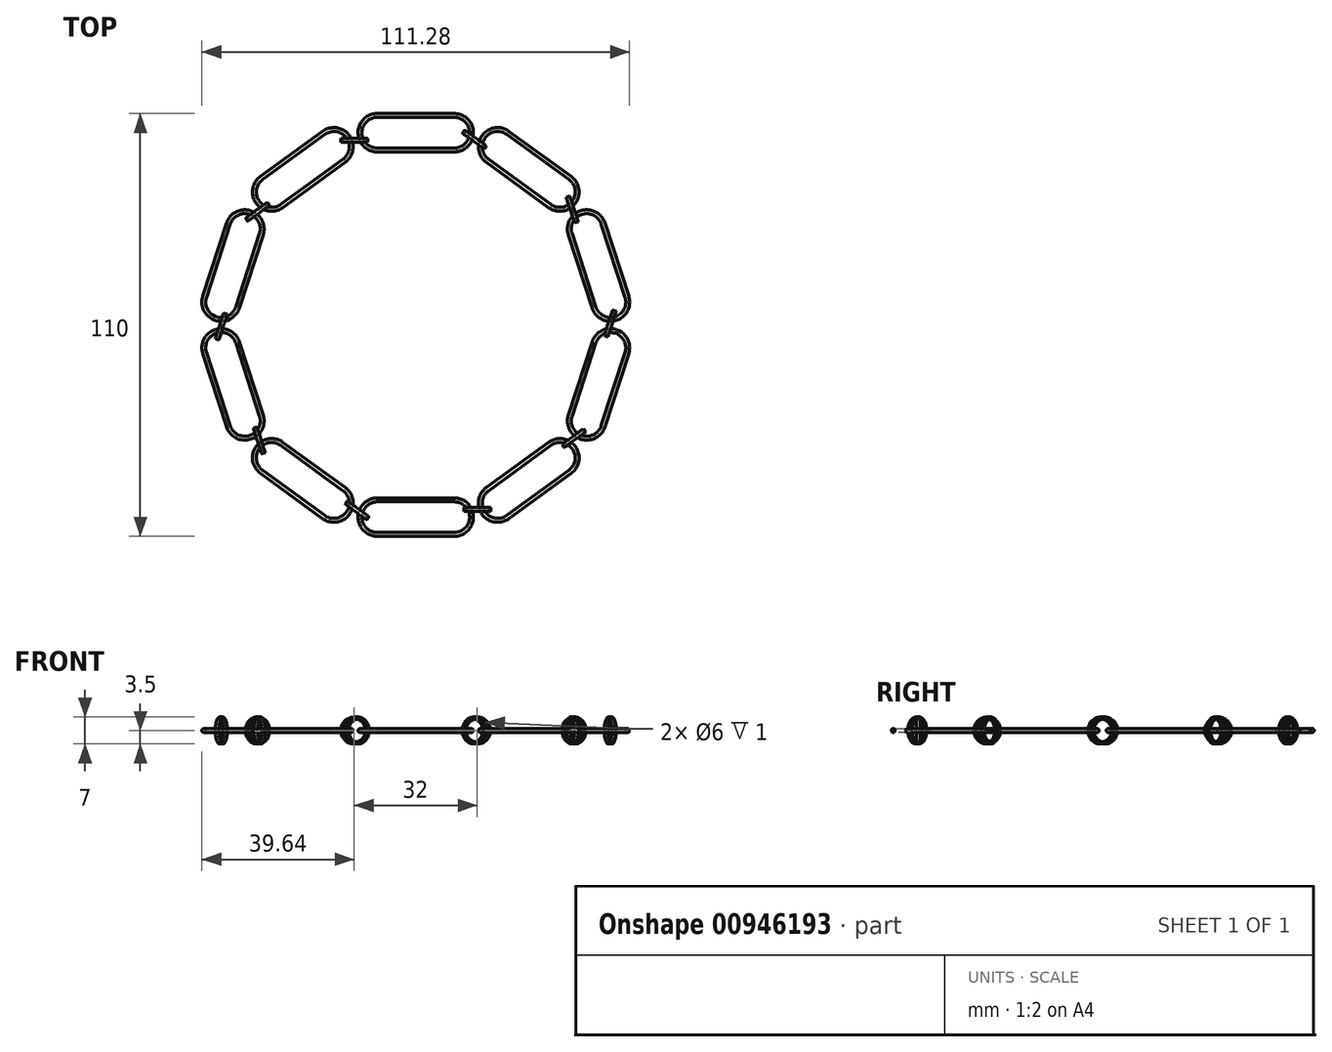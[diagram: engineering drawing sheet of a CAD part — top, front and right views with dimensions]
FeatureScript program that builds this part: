
annotation { "Feature Type Name" : "Feature", "Feature Type Description" : "" }
export const myFeature = defineFeature(function(context is Context, id is Id, definition is map)
    precondition{}
    {
        {
            var Q0;
            Q0=qCreatedBy(makeId("Top.planeOp"),FACE);
            var sketch = newSketch(context, id + "F0", { "sketchPlane" : qUnion([Q0])});
            skArc(sketch, "E0", {"start": v(-10, -45) * mm, "mid": v(-15, -50) * mm, "end": v(-10, -55) * mm});
            skArc(sketch, "E1", {"start": v(10, -55) * mm, "mid": v(15, -50) * mm, "end": v(10, -45) * mm});
            skLineSegment(sketch, "E2", {"start": v(-10, -45) * mm, "end": v(10, -45) * mm});
            skLineSegment(sketch, "E3", {"start": v(-10, -55) * mm, "end": v(10, -55) * mm});
            skLineSegment(sketch, "E4", {"start": v(-10, -50) * mm, "end": v(10, -50) * mm, "construction": true});
            skPoint(sketch, "E5", {"position": v(0, -50) * mm});
            skArc(sketch, "E6.0", {"start": v(-10, -46) * mm, "mid": v(-14, -50) * mm, "end": v(-10, -54) * mm});
            skLineSegment(sketch, "E6.1", {"start": v(-10, -46) * mm, "end": v(10, -46) * mm});
            skArc(sketch, "E6.2", {"start": v(10, -54) * mm, "mid": v(14, -50) * mm, "end": v(10, -46) * mm});
            skLineSegment(sketch, "E6.3", {"start": v(-10, -54) * mm, "end": v(10, -54) * mm});
            skSolve(sketch);
        }
        {
            var Q0;
            Q0 = qSketchRegion(id + "F0", true);
            extrude(context, id + "F1", {"entities" : qUnion([Q0]), "depth" : 1 * mm, "offsetDistance" : 25 * mm});
        }
        {
            var Q0;
            Q0=makeQuery(id+"F1.opExtrude","CAP_FACE",FACE,{"disambiguationData":[OSD([sQuery(id+"F0.wireOp",EDGE,"E0"),sQuery(id+"F0.wireOp",EDGE,"E1"),sQuery(id+"F0.wireOp",EDGE,"E2"),sQuery(id+"F0.wireOp",EDGE,"E3"),sQuery(id+"F0.wireOp",EDGE,"E6.0"),sQuery(id+"F0.wireOp",EDGE,"E6.1"),sQuery(id+"F0.wireOp",EDGE,"E6.2"),sQuery(id+"F0.wireOp",EDGE,"E6.3")])],"isStart":true});
            var Q1;
            Q1=makeQuery(id+"F1.opExtrude","CAP_FACE",FACE,{"disambiguationData":[OSD([sQuery(id+"F0.wireOp",EDGE,"E0"),sQuery(id+"F0.wireOp",EDGE,"E1"),sQuery(id+"F0.wireOp",EDGE,"E2"),sQuery(id+"F0.wireOp",EDGE,"E3"),sQuery(id+"F0.wireOp",EDGE,"E6.0"),sQuery(id+"F0.wireOp",EDGE,"E6.1"),sQuery(id+"F0.wireOp",EDGE,"E6.2"),sQuery(id+"F0.wireOp",EDGE,"E6.3")])],"isStart":false});
            fillet(context, id + "F2", {"entities" : qUnion([Q0, Q1]), "radius" : 0.5 * mm, "tangentPropagation" : true, "allowEdgeOverflow" : false});
        }
        {
            var Q0;
            Q0=qCreatedBy(makeId("Front.planeOp"),FACE);
            cPlane(context, id + "F3", {"entities" : qUnion([Q0]), "cplaneType" : CPlaneType.OFFSET, "offset" : 48 * mm, "width" : 150 * mm, "height" : 150 * mm});
        }
        {
            var Q0;
            Q0=qCreatedBy(id+"F3.planeOp",FACE);
            var sketch = newSketch(context, id + "F4", { "sketchPlane" : qUnion([Q0])});
            skCircle(sketch, "E7", {"center": v(16, 0.5) * mm, "radius": 3.5 * mm});
            skCircle(sketch, "E8", {"center": v(16, 0.5) * mm, "radius": 3 * mm});
            skSolve(sketch);
        }
        {
            var Q0;
            Q0=makeQuery(id+"F4.imprint","IMPRINT",FACE,{"disambiguationData":[TD([[makeQuery(id+"F4.imprint","IMPRINT",EDGE,{"derivedFrom":sQuery(id+"F4.wireOp",EDGE,"E7")}),1.0]])]});
            extrude(context, id + "F5", {"entities" : qUnion([Q0]), "endBound" : BoundingType.SYMMETRIC, "depth" : 1 * mm, "offsetDistance" : 25 * mm});
        }
        {
            var Q0;
            Q0=qCreatedBy(makeId("Front.planeOp"),FACE);
            var sketch = newSketch(context, id + "F6", { "sketchPlane" : qUnion([Q0])});
            skLineSegment(sketch, "E9", {"start": v(0, 6.36) * mm, "end": v(0, -4.68) * mm, "construction": true});
            skSolve(sketch);
        }
        {
            var Q0;
            Q0=makeQuery(id+"F1.opExtrude","SWEPT_BODY",BODY,{"disambiguationData":[OSD([sQuery(id+"F0.wireOp",EDGE,"E0"),sQuery(id+"F0.wireOp",EDGE,"E1"),sQuery(id+"F0.wireOp",EDGE,"E2"),sQuery(id+"F0.wireOp",EDGE,"E3"),sQuery(id+"F0.wireOp",EDGE,"E6.0"),sQuery(id+"F0.wireOp",EDGE,"E6.1"),sQuery(id+"F0.wireOp",EDGE,"E6.2"),sQuery(id+"F0.wireOp",EDGE,"E6.3")])]});
            var Q1;
            Q1=makeQuery(id+"F5.opExtrude","SWEPT_BODY",BODY,{"disambiguationData":[OSD([sQuery(id+"F4.wireOp",EDGE,"E7"),sQuery(id+"F4.wireOp",EDGE,"E8")])]});
            var Q2;
            Q2=sQuery(id+"F6.wireOp",EDGE,"E9");
            circularPattern(context, id + "F7", {"entities" : qUnion([Q0, Q1]), "axis" : qUnion([Q2]), "angle" : 360 * degree, "instanceCount" : 10, "equalSpace" : true});
        }
    });
